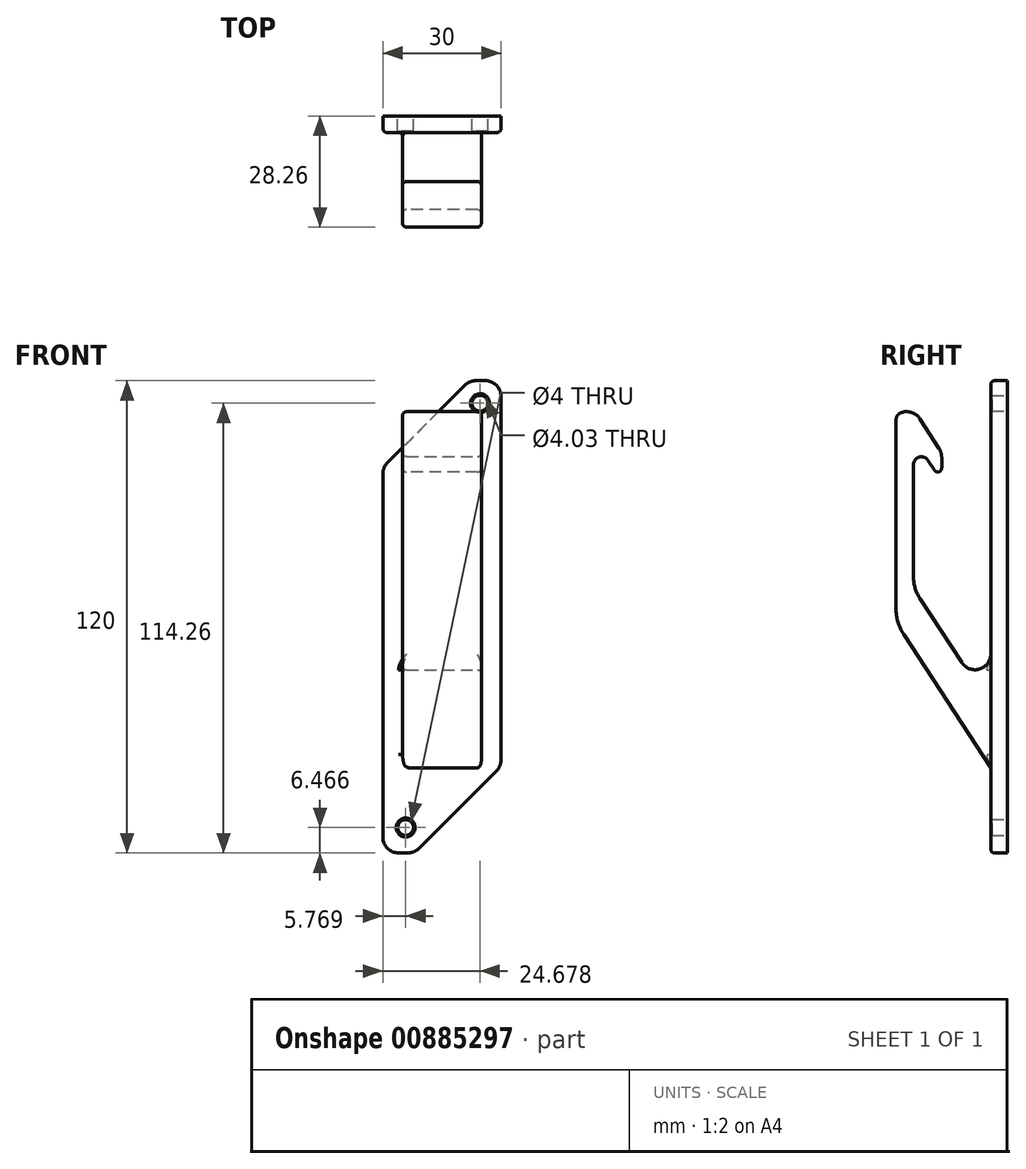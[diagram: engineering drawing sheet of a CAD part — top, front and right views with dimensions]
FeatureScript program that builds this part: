
annotation { "Feature Type Name" : "Feature", "Feature Type Description" : "" }
export const myFeature = defineFeature(function(context is Context, id is Id, definition is map)
    precondition{}
    {
        {
            var Q0;
            Q0=qCreatedBy(makeId("Front.planeOp"),FACE);
            var sketch = newSketch(context, id + "F0", { "sketchPlane" : qUnion([Q0])});
            skLineSegment(sketch, "E0.bottom", {"start": v(15, 60) * mm, "end": v(-15, 60) * mm});
            skLineSegment(sketch, "E0.top", {"start": v(15, -60) * mm, "end": v(-15, -60) * mm});
            skLineSegment(sketch, "E0.left", {"start": v(15, 60) * mm, "end": v(15, -60) * mm});
            skLineSegment(sketch, "E0.right", {"start": v(-15, 60) * mm, "end": v(-15, -60) * mm});
            skPoint(sketch, "E0.middle", {"position": v(0, 0) * mm});
            skSolve(sketch);
        }
        {
            var Q0;
            Q0 = qSketchRegion(id + "F0", true);
            extrude(context, id + "F1", {"entities" : qUnion([Q0]), "depth" : 4.2 * mm, "offsetDistance" : 25 * mm});
        }
        {
            var Q0;
            Q0=makeQuery(id+"F1.opExtrude","SWEPT_EDGE",EDGE,{"disambiguationData":[OSD([sQuery(id+"F0.wireOp",EDGE,"E0.top"),sQuery(id+"F0.wireOp",EDGE,"E0.left")])]});
            chamfer(context, id + "F2", {"entities" : qUnion([Q0]), "width" : 22 * mm, "tangentPropagation" : true});
        }
        {
            var Q0;
            Q0=makeQuery(id+"F1.opExtrude","SWEPT_EDGE",EDGE,{"disambiguationData":[OSD([sQuery(id+"F0.wireOp",EDGE,"E0.bottom"),sQuery(id+"F0.wireOp",EDGE,"E0.right")])]});
            chamfer(context, id + "F3", {"entities" : qUnion([Q0]), "width" : 22 * mm, "tangentPropagation" : true});
        }
        {
            var Q0;
            {var subQ0=sQuery(id+"F0.wireOp",EDGE,"E0.right");Q0=makeQuery(id+"F3.opChamfer","BLEND_EDGE",EDGE,{"blendedFrom":[makeQuery(id+"F1.opExtrude","SWEPT_EDGE",EDGE,{"disambiguationData":[OSD([sQuery(id+"F0.wireOp",EDGE,"E0.bottom"),subQ0])]}),makeQuery(id+"F1.opExtrude","SWEPT_FACE",FACE,{"disambiguationData":[OSD([subQ0])]})],"blendedInto":[makeQuery(id+"F1.opExtrude","SWEPT_FACE",FACE,{"disambiguationData":[OSD([subQ0])]})]});}
            var Q1;
            {var subQ0=sQuery(id+"F0.wireOp",EDGE,"E0.bottom");Q1=makeQuery(id+"F3.opChamfer","BLEND_EDGE",EDGE,{"blendedFrom":[makeQuery(id+"F1.opExtrude","SWEPT_EDGE",EDGE,{"disambiguationData":[OSD([subQ0,sQuery(id+"F0.wireOp",EDGE,"E0.right")])]}),makeQuery(id+"F1.opExtrude","SWEPT_FACE",FACE,{"disambiguationData":[OSD([subQ0])]})],"blendedInto":[makeQuery(id+"F1.opExtrude","SWEPT_FACE",FACE,{"disambiguationData":[OSD([subQ0])]})]});}
            var Q2;
            Q2=makeQuery(id+"F1.opExtrude","SWEPT_EDGE",EDGE,{"disambiguationData":[OSD([sQuery(id+"F0.wireOp",EDGE,"E0.bottom"),sQuery(id+"F0.wireOp",EDGE,"E0.left")])]});
            var Q3;
            {var subQ0=sQuery(id+"F0.wireOp",EDGE,"E0.left");Q3=makeQuery(id+"F2.opChamfer","BLEND_EDGE",EDGE,{"blendedFrom":[makeQuery(id+"F1.opExtrude","SWEPT_EDGE",EDGE,{"disambiguationData":[OSD([sQuery(id+"F0.wireOp",EDGE,"E0.top"),subQ0])]}),makeQuery(id+"F1.opExtrude","SWEPT_FACE",FACE,{"disambiguationData":[OSD([subQ0])]})],"blendedInto":[makeQuery(id+"F1.opExtrude","SWEPT_FACE",FACE,{"disambiguationData":[OSD([subQ0])]})]});}
            var Q4;
            {var subQ0=sQuery(id+"F0.wireOp",EDGE,"E0.top");Q4=makeQuery(id+"F2.opChamfer","BLEND_EDGE",EDGE,{"blendedFrom":[makeQuery(id+"F1.opExtrude","SWEPT_EDGE",EDGE,{"disambiguationData":[OSD([subQ0,sQuery(id+"F0.wireOp",EDGE,"E0.left")])]}),makeQuery(id+"F1.opExtrude","SWEPT_FACE",FACE,{"disambiguationData":[OSD([subQ0])]})],"blendedInto":[makeQuery(id+"F1.opExtrude","SWEPT_FACE",FACE,{"disambiguationData":[OSD([subQ0])]})]});}
            var Q5;
            Q5=makeQuery(id+"F1.opExtrude","SWEPT_EDGE",EDGE,{"disambiguationData":[OSD([sQuery(id+"F0.wireOp",EDGE,"E0.top"),sQuery(id+"F0.wireOp",EDGE,"E0.right")])]});
            fillet(context, id + "F4", {"entities" : qUnion([Q0, Q1, Q2, Q3, Q4, Q5]), "radius" : 4 * mm, "tangentPropagation" : true, "allowEdgeOverflow" : false});
        }
        {
            var Q0;
            Q0=makeQuery(id+"F1.opExtrude","CAP_EDGE",EDGE,{"disambiguationData":[OSD([sQuery(id+"F0.wireOp",EDGE,"E0.left")])],"isStart":false});
            var Q1;
            {var subQ0=sQuery(id+"F0.wireOp",EDGE,"E0.right");var subQ1=sQuery(id+"F0.wireOp",EDGE,"E0.bottom");Q1=makeQuery(id+"F3.opChamfer","BLEND_EDGE",EDGE,{"blendedFrom":[makeQuery(id+"F1.opExtrude","SWEPT_EDGE",EDGE,{"disambiguationData":[OSD([subQ1,subQ0])]}),makeQuery(id+"F1.opExtrude","CAP_FACE",FACE,{"disambiguationData":[OSD([subQ1,sQuery(id+"F0.wireOp",EDGE,"E0.top"),sQuery(id+"F0.wireOp",EDGE,"E0.left"),subQ0])],"isStart":false})],"blendedInto":[makeQuery(id+"F1.opExtrude","CAP_FACE",FACE,{"disambiguationData":[OSD([subQ1,sQuery(id+"F0.wireOp",EDGE,"E0.top"),sQuery(id+"F0.wireOp",EDGE,"E0.left"),subQ0])],"isStart":false})]});}
            var Q2;
            Q2=makeQuery(id+"F7.opExtrude","CAP_EDGE",EDGE,{"disambiguationData":[OSD([sQuery(id+"F6.wireOp",EDGE,"E1")])],"isStart":false});
            var Q3;
            Q3=makeQuery(id+"F7.opExtrude","CAP_EDGE",EDGE,{"disambiguationData":[OSD([sQuery(id+"F6.wireOp",EDGE,"E2")])],"isStart":true});
            var Q4;
            Q4=makeQuery(id+"F7.boolean.opBoolean","INTERSECT",EDGE,{"derivedFrom":[makeQuery(id+"F1.opExtrude","CAP_FACE",FACE,{"disambiguationData":[OSD([sQuery(id+"F0.wireOp",EDGE,"E0.bottom"),sQuery(id+"F0.wireOp",EDGE,"E0.top"),sQuery(id+"F0.wireOp",EDGE,"E0.left"),sQuery(id+"F0.wireOp",EDGE,"E0.right")])],"isStart":false}),makeQuery(id+"F7.opExtrude","CAP_FACE",FACE,{"disambiguationData":[OSD([sQuery(id+"F6.wireOp",EDGE,"E1"),sQuery(id+"F6.wireOp",EDGE,"E2"),sQuery(id+"F6.wireOp",EDGE,"E3"),sQuery(id+"F6.wireOp",EDGE,"E4"),sQuery(id+"F6.wireOp",EDGE,"E5"),sQuery(id+"F6.wireOp",EDGE,"E6"),sQuery(id+"F6.wireOp",EDGE,"E7"),sQuery(id+"F6.wireOp",EDGE,"E8"),sQuery(id+"F6.wireOp",EDGE,"E9")])],"isStart":true})]});
            fillet(context, id + "F5", {"entities" : qUnion([Q0, Q1, Q2, Q3, Q4]), "radius" : 1 * mm, "tangentPropagation" : true, "allowEdgeOverflow" : false});
        }
        {
            var Q0;
            Q0=qCreatedBy(makeId("Right.planeOp"),FACE);
            var sketch = newSketch(context, id + "F6", { "sketchPlane" : qUnion([Q0])});
            skLineSegment(sketch, "E1", {"start": v(-4.03, -38.6) * mm, "end": v(-28.26, -1.46) * mm});
            skLineSegment(sketch, "E2", {"start": v(-28.26, -1.46) * mm, "end": v(-28.26, 51.04) * mm});
            skLineSegment(sketch, "E3", {"start": v(-28.26, 51.04) * mm, "end": v(-25.6, 55.54) * mm});
            skLineSegment(sketch, "E4", {"start": v(-25.6, 55.54) * mm, "end": v(-16.66, 41.82) * mm});
            skLineSegment(sketch, "E5", {"start": v(-16.66, 41.82) * mm, "end": v(-16.66, 34.43) * mm});
            skLineSegment(sketch, "E6", {"start": v(-16.66, 34.43) * mm, "end": v(-23.82, 45.4) * mm});
            skLineSegment(sketch, "E7", {"start": v(-23.82, 45.4) * mm, "end": v(-23.82, 7.17) * mm});
            skLineSegment(sketch, "E8", {"start": v(-23.82, 7.17) * mm, "end": v(-4.03, -23.16) * mm});
            skLineSegment(sketch, "E9", {"start": v(-4.03, -23.16) * mm, "end": v(-4.03, -38.6) * mm});
            skSolve(sketch);
        }
        {
            var Q0;
            Q0 = qSketchRegion(id + "F6", true);
            extrude(context, id + "F7", {"entities" : qUnion([Q0]), "operationType" : NewBodyOperationType.ADD, "depth" : 10 * mm, "offsetDistance" : 25 * mm, "hasSecondDirection" : true, "secondDirectionOppositeDirection" : true, "secondDirectionDepth" : 10 * mm});
        }
        {
            var Q0;
            Q0=makeQuery(id+"F7.boolean.opBoolean","INTERSECT",EDGE,{"derivedFrom":[makeQuery(id+"F1.opExtrude","CAP_FACE",FACE,{"disambiguationData":[OSD([sQuery(id+"F0.wireOp",EDGE,"E0.bottom"),sQuery(id+"F0.wireOp",EDGE,"E0.top"),sQuery(id+"F0.wireOp",EDGE,"E0.left"),sQuery(id+"F0.wireOp",EDGE,"E0.right")])],"isStart":false}),makeQuery(id+"F7.opExtrude","SWEPT_FACE",FACE,{"disambiguationData":[OSD([sQuery(id+"F6.wireOp",EDGE,"E8")])]})]});
            fillet(context, id + "F8", {"entities" : qUnion([Q0]), "radius" : 4 * mm, "tangentPropagation" : true, "allowEdgeOverflow" : false});
        }
        {
            var Q0;
            Q0=makeQuery(id+"F7.opExtrude","SWEPT_EDGE",EDGE,{"disambiguationData":[OSD([sQuery(id+"F6.wireOp",EDGE,"E7"),sQuery(id+"F6.wireOp",EDGE,"E8")])]});
            fillet(context, id + "F9", {"entities" : qUnion([Q0]), "radius" : 10 * mm, "tangentPropagation" : true, "allowEdgeOverflow" : false});
        }
        {
            var Q0;
            Q0=makeQuery(id+"F7.opExtrude","SWEPT_EDGE",EDGE,{"disambiguationData":[OSD([sQuery(id+"F6.wireOp",EDGE,"E6"),sQuery(id+"F6.wireOp",EDGE,"E7")])]});
            fillet(context, id + "F10", {"entities" : qUnion([Q0]), "radius" : 2 * mm, "tangentPropagation" : true, "allowEdgeOverflow" : false});
        }
        {
            var Q0;
            Q0=makeQuery(id+"F7.opExtrude","SWEPT_EDGE",EDGE,{"disambiguationData":[OSD([sQuery(id+"F6.wireOp",EDGE,"E3"),sQuery(id+"F6.wireOp",EDGE,"E4")])]});
            fillet(context, id + "F11", {"entities" : qUnion([Q0]), "radius" : 4 * mm, "tangentPropagation" : true, "allowEdgeOverflow" : false});
        }
        {
            var Q0;
            Q0=makeQuery(id+"F11.opFillet","BLEND_EDGE",EDGE,{"blendedFrom":[makeQuery(id+"F7.opExtrude","SWEPT_EDGE",EDGE,{"disambiguationData":[OSD([sQuery(id+"F6.wireOp",EDGE,"E3"),sQuery(id+"F6.wireOp",EDGE,"E4")])]}),makeQuery(id+"F7.opExtrude","SWEPT_FACE",FACE,{"disambiguationData":[OSD([sQuery(id+"F6.wireOp",EDGE,"E2")])]})],"blendedInto":[makeQuery(id+"F7.opExtrude","SWEPT_FACE",FACE,{"disambiguationData":[OSD([sQuery(id+"F6.wireOp",EDGE,"E2")])]})]});
            fillet(context, id + "F12", {"entities" : qUnion([Q0]), "radius" : 2 * mm, "tangentPropagation" : true, "allowEdgeOverflow" : false});
        }
        {
            var Q0;
            Q0=makeQuery(id+"F7.opExtrude","SWEPT_EDGE",EDGE,{"disambiguationData":[OSD([sQuery(id+"F6.wireOp",EDGE,"E4"),sQuery(id+"F6.wireOp",EDGE,"E5")])]});
            fillet(context, id + "F13", {"entities" : qUnion([Q0]), "radius" : 4 * mm, "tangentPropagation" : true, "allowEdgeOverflow" : false});
        }
        {
            var Q0;
            Q0=makeQuery(id+"F7.opExtrude","SWEPT_EDGE",EDGE,{"disambiguationData":[OSD([sQuery(id+"F6.wireOp",EDGE,"E5"),sQuery(id+"F6.wireOp",EDGE,"E6")])]});
            fillet(context, id + "F14", {"entities" : qUnion([Q0]), "radius" : 1 * mm, "tangentPropagation" : true, "allowEdgeOverflow" : false});
        }
        {
            var Q0;
            Q0=makeQuery(id+"F7.opExtrude","SWEPT_EDGE",EDGE,{"disambiguationData":[OSD([sQuery(id+"F6.wireOp",EDGE,"E1"),sQuery(id+"F6.wireOp",EDGE,"E2")])]});
            fillet(context, id + "F15", {"entities" : qUnion([Q0]), "radius" : 12 * mm, "tangentPropagation" : true, "allowEdgeOverflow" : false});
        }
        {
            var Q0;
            Q0=qCreatedBy(makeId("Front.planeOp"),FACE);
            var sketch = newSketch(context, id + "F16", { "sketchPlane" : qUnion([Q0])});
            skCircle(sketch, "E10", {"center": v(9.68, 54.26) * mm, "radius": 2.01 * mm});
            skCircle(sketch, "E11", {"center": v(-9.23, -53.53) * mm, "radius": 2 * mm});
            skSolve(sketch);
        }
        {
            var Q0;
            Q0 = qSketchRegion(id + "F16", true);
            extrude(context, id + "F17", {"entities" : qUnion([Q0]), "operationType" : NewBodyOperationType.REMOVE, "depth" : 25 * mm, "offsetDistance" : 25 * mm});
        }
        {
            var Q0;
            Q0=makeQuery(id+"F17.boolean.opBoolean","INTERSECT",EDGE,{"derivedFrom":[makeQuery(id+"F1.opExtrude","CAP_FACE",FACE,{"disambiguationData":[OSD([sQuery(id+"F0.wireOp",EDGE,"E0.bottom"),sQuery(id+"F0.wireOp",EDGE,"E0.top"),sQuery(id+"F0.wireOp",EDGE,"E0.left"),sQuery(id+"F0.wireOp",EDGE,"E0.right")])],"isStart":false}),makeQuery(id+"F17.opExtrude","SWEPT_FACE",FACE,{"disambiguationData":[OSD([sQuery(id+"F16.wireOp",EDGE,"E10")])]})]});
            var Q1;
            Q1=makeQuery(id+"F17.boolean.opBoolean","INTERSECT",EDGE,{"derivedFrom":[makeQuery(id+"F1.opExtrude","CAP_FACE",FACE,{"disambiguationData":[OSD([sQuery(id+"F0.wireOp",EDGE,"E0.bottom"),sQuery(id+"F0.wireOp",EDGE,"E0.top"),sQuery(id+"F0.wireOp",EDGE,"E0.left"),sQuery(id+"F0.wireOp",EDGE,"E0.right")])],"isStart":false}),makeQuery(id+"F17.opExtrude","SWEPT_FACE",FACE,{"disambiguationData":[OSD([sQuery(id+"F16.wireOp",EDGE,"E11")])]})]});
            chamfer(context, id + "F18", {"entities" : qUnion([Q0, Q1]), "width" : .4 * mm, "tangentPropagation" : true});
        }
        {
            var Q0;
            Q0=makeQuery(id+"F7.opExtrude","CAP_EDGE",EDGE,{"disambiguationData":[OSD([sQuery(id+"F6.wireOp",EDGE,"E2")])],"isStart":true});
            var Q1;
            Q1=makeQuery(id+"F7.opExtrude","CAP_EDGE",EDGE,{"disambiguationData":[OSD([sQuery(id+"F6.wireOp",EDGE,"E2")])],"isStart":false});
            var Q2;
            Q2=makeQuery(id+"F7.boolean.opBoolean","INTERSECT",EDGE,{"derivedFrom":[makeQuery(id+"F1.opExtrude","CAP_FACE",FACE,{"disambiguationData":[OSD([sQuery(id+"F0.wireOp",EDGE,"E0.bottom"),sQuery(id+"F0.wireOp",EDGE,"E0.top"),sQuery(id+"F0.wireOp",EDGE,"E0.left"),sQuery(id+"F0.wireOp",EDGE,"E0.right")])],"isStart":false}),makeQuery(id+"F7.opExtrude","CAP_FACE",FACE,{"disambiguationData":[OSD([sQuery(id+"F6.wireOp",EDGE,"E1"),sQuery(id+"F6.wireOp",EDGE,"E2"),sQuery(id+"F6.wireOp",EDGE,"E3"),sQuery(id+"F6.wireOp",EDGE,"E4"),sQuery(id+"F6.wireOp",EDGE,"E5"),sQuery(id+"F6.wireOp",EDGE,"E6"),sQuery(id+"F6.wireOp",EDGE,"E7"),sQuery(id+"F6.wireOp",EDGE,"E8"),sQuery(id+"F6.wireOp",EDGE,"E9")])],"isStart":true})]});
            fillet(context, id + "F19", {"entities" : qUnion([Q0, Q1, Q2]), "radius" : 1 * mm, "tangentPropagation" : true, "allowEdgeOverflow" : false});
        }
    });
